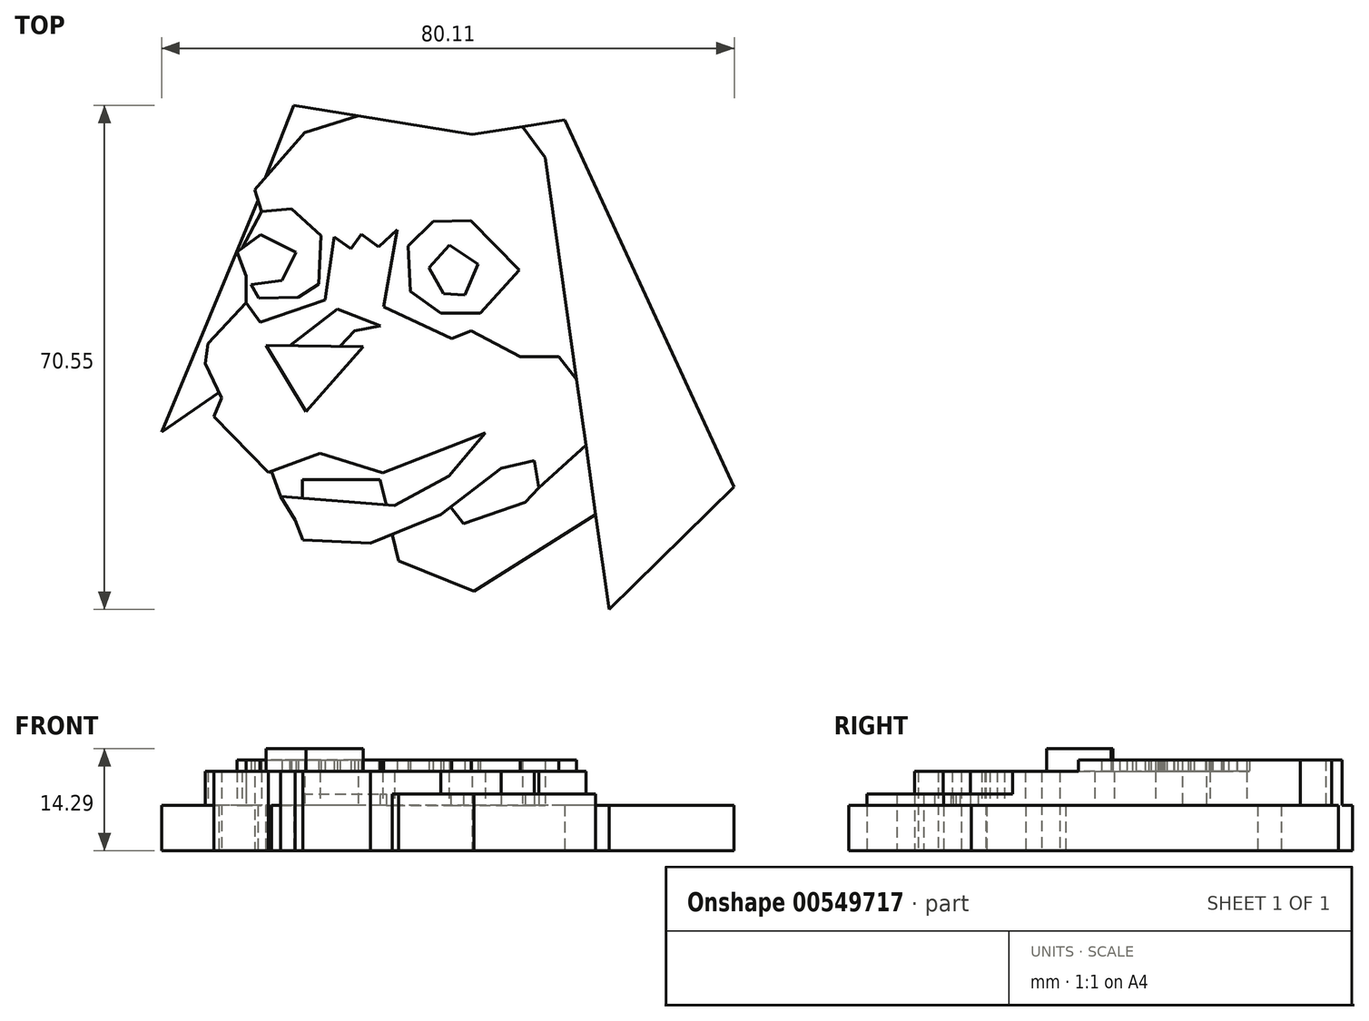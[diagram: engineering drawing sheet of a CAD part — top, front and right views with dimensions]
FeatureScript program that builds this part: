
annotation { "Feature Type Name" : "Feature", "Feature Type Description" : "" }
export const myFeature = defineFeature(function(context is Context, id is Id, definition is map)
    precondition{}
    {
        {
            var Q0;
            Q0=qCreatedBy(makeId("Top.planeOp"),FACE);
            var sketch = newSketch(context, id + "F0", { "sketchPlane" : qUnion([Q0])});
            skLineSegment(sketch, "E0", {"start": v(-28.92, 19.78) * mm, "end": v(-27.96, 16.71) * mm});
            skLineSegment(sketch, "E1", {"start": v(-27.96, 16.71) * mm, "end": v(-23.77, 17.1) * mm});
            skLineSegment(sketch, "E2", {"start": v(-23.77, 17.1) * mm, "end": v(-19.66, 13.35) * mm});
            skLineSegment(sketch, "E3", {"start": v(-19.66, 13.35) * mm, "end": v(-19.93, 6.56) * mm});
            skLineSegment(sketch, "E4", {"start": v(-19.93, 6.56) * mm, "end": v(-22.81, 4.73) * mm});
            skLineSegment(sketch, "E5", {"start": v(-22.81, 4.73) * mm, "end": v(-28.35, 4.56) * mm});
            skLineSegment(sketch, "E6", {"start": v(-28.35, 4.56) * mm, "end": v(-30.1, 7.71) * mm});
            skLineSegment(sketch, "E7", {"start": v(-30.1, 7.71) * mm, "end": v(-30.1, 3.95) * mm});
            skLineSegment(sketch, "E8", {"start": v(-30.1, 7.71) * mm, "end": v(-31.36, 11.09) * mm});
            skLineSegment(sketch, "E9", {"start": v(-31.36, 11.09) * mm, "end": v(-28.1, 13.47) * mm});
            skLineSegment(sketch, "E10", {"start": v(-28.1, 13.47) * mm, "end": v(-23.11, 10.99) * mm});
            skLineSegment(sketch, "E11", {"start": v(-23.11, 10.99) * mm, "end": v(-25.06, 7.08) * mm});
            skLineSegment(sketch, "E12", {"start": v(-25.06, 7.08) * mm, "end": v(-29.42, 6.49) * mm});
            skLineSegment(sketch, "E13", {"start": v(-27.96, 16.71) * mm, "end": v(-30.7, 11.57) * mm});
            skLineSegment(sketch, "E14", {"start": v(-28.44, 18.25) * mm, "end": v(-41.92, -14.16) * mm});
            skLineSegment(sketch, "E15", {"start": v(-41.92, -14.16) * mm, "end": v(-33.9, -8.63) * mm});
            skLineSegment(sketch, "E16", {"start": v(-33.9, -8.63) * mm, "end": v(-35.81, -4.56) * mm});
            skLineSegment(sketch, "E17", {"start": v(-35.81, -4.56) * mm, "end": v(-35.46, -1.8) * mm});
            skLineSegment(sketch, "E18", {"start": v(-35.46, -1.8) * mm, "end": v(-30.1, 3.95) * mm});
            skLineSegment(sketch, "E19", {"start": v(-30.1, 3.95) * mm, "end": v(-28.12, 1.24) * mm});
            skLineSegment(sketch, "E20", {"start": v(-28.12, 1.24) * mm, "end": v(-19.08, 4.3) * mm});
            skLineSegment(sketch, "E21", {"start": v(-19.08, 4.3) * mm, "end": v(-17.81, 13.18) * mm});
            skLineSegment(sketch, "E22", {"start": v(-17.81, 13.18) * mm, "end": v(-15.44, 11.49) * mm});
            skLineSegment(sketch, "E23", {"start": v(-15.44, 11.49) * mm, "end": v(-14, 13.5) * mm});
            skLineSegment(sketch, "E24", {"start": v(-14, 13.5) * mm, "end": v(-11.55, 11.76) * mm});
            skLineSegment(sketch, "E25", {"start": v(-11.55, 11.76) * mm, "end": v(-8.94, 14.17) * mm});
            skLineSegment(sketch, "E26", {"start": v(-8.94, 14.17) * mm, "end": v(-10.88, 3.37) * mm});
            skLineSegment(sketch, "E27", {"start": v(-10.88, 3.37) * mm, "end": v(-1.34, -1.04) * mm});
            skLineSegment(sketch, "E28", {"start": v(-1.34, -1.04) * mm, "end": v(1.4, 0) * mm});
            skLineSegment(sketch, "E29", {"start": v(1.4, 0) * mm, "end": v(8.24, -3.6) * mm});
            skLineSegment(sketch, "E30", {"start": v(8.24, -3.6) * mm, "end": v(13.64, -3.6) * mm});
            skLineSegment(sketch, "E31", {"start": v(13.64, -3.6) * mm, "end": v(16.12, -6.8) * mm});
            skLineSegment(sketch, "E32", {"start": v(11.71, 24.26) * mm, "end": v(20.68, -38.98) * mm});
            skLineSegment(sketch, "E33", {"start": v(20.68, -38.98) * mm, "end": v(38.19, -21.8) * mm});
            skLineSegment(sketch, "E34", {"start": v(38.19, -21.8) * mm, "end": v(14.47, 29.55) * mm});
            skLineSegment(sketch, "E35", {"start": v(14.47, 29.55) * mm, "end": v(1.52, 27.5) * mm});
            skLineSegment(sketch, "E36", {"start": v(4.12, 27.08) * mm, "end": v(-23.44, 31.57) * mm});
            skLineSegment(sketch, "E37", {"start": v(-23.44, 31.57) * mm, "end": v(-27.48, 21.27) * mm});
            skLineSegment(sketch, "E38", {"start": v(-28.92, 19.78) * mm, "end": v(-21.91, 27.77) * mm});
            skLineSegment(sketch, "E39", {"start": v(-21.91, 27.77) * mm, "end": v(-14.43, 30.1) * mm});
            skLineSegment(sketch, "E40", {"start": v(7.07, 24.85) * mm, "end": v(11.71, 24.26) * mm});
            skLineSegment(sketch, "E41", {"start": v(-7.46, 11.9) * mm, "end": v(-3.96, 15.32) * mm});
            skLineSegment(sketch, "E42", {"start": v(-3.96, 15.32) * mm, "end": v(1.35, 15.44) * mm});
            skLineSegment(sketch, "E43", {"start": v(1.35, 15.44) * mm, "end": v(8.1, 8.52) * mm});
            skLineSegment(sketch, "E44", {"start": v(8.1, 8.52) * mm, "end": v(2.67, 2.5) * mm});
            skLineSegment(sketch, "E45", {"start": v(2.67, 2.5) * mm, "end": v(-2.9, 2.5) * mm});
            skLineSegment(sketch, "E46", {"start": v(-2.9, 2.5) * mm, "end": v(-7.12, 5.55) * mm});
            skLineSegment(sketch, "E47", {"start": v(-7.12, 5.55) * mm, "end": v(-7.46, 11.9) * mm});
            skLineSegment(sketch, "E48", {"start": v(-4.5, 8.85) * mm, "end": v(-1.65, 12) * mm});
            skLineSegment(sketch, "E49", {"start": v(-1.65, 12) * mm, "end": v(2.34, 9.35) * mm});
            skLineSegment(sketch, "E50", {"start": v(2.34, 9.35) * mm, "end": v(0.52, 5) * mm});
            skLineSegment(sketch, "E51", {"start": v(0.52, 5) * mm, "end": v(-2.48, 5.22) * mm});
            skLineSegment(sketch, "E52", {"start": v(-2.48, 5.22) * mm, "end": v(-4.5, 8.85) * mm});
            skLineSegment(sketch, "E53", {"start": v(-32.42, -6.74) * mm, "end": v(-34.61, -11.98) * mm});
            skLineSegment(sketch, "E54", {"start": v(-34.61, -11.98) * mm, "end": v(-26.99, -19.8) * mm});
            skLineSegment(sketch, "E55", {"start": v(-26.99, -19.8) * mm, "end": v(-19.76, -17.15) * mm});
            skLineSegment(sketch, "E56", {"start": v(-19.76, -17.15) * mm, "end": v(-11.02, -19.87) * mm});
            skLineSegment(sketch, "E57", {"start": v(-11.02, -19.87) * mm, "end": v(3.38, -14.27) * mm});
            skLineSegment(sketch, "E58", {"start": v(3.38, -14.27) * mm, "end": v(-1.71, -20.33) * mm});
            skLineSegment(sketch, "E59", {"start": v(-1.71, -20.33) * mm, "end": v(-9.37, -24.45) * mm});
            skLineSegment(sketch, "E60", {"start": v(-9.37, -24.45) * mm, "end": v(-25.28, -23.17) * mm});
            skLineSegment(sketch, "E61", {"start": v(-25.28, -23.17) * mm, "end": v(-26.57, -19.65) * mm});
            skLineSegment(sketch, "E62", {"start": v(-22.25, -23.41) * mm, "end": v(-22.25, -20.84) * mm});
            skLineSegment(sketch, "E63", {"start": v(-22.25, -20.84) * mm, "end": v(-11.39, -20.84) * mm});
            skLineSegment(sketch, "E64", {"start": v(-11.39, -20.84) * mm, "end": v(-10.5, -24.36) * mm});
            skLineSegment(sketch, "E65", {"start": v(-25.28, -23.17) * mm, "end": v(-23.24, -26.44) * mm});
            skLineSegment(sketch, "E66", {"start": v(-23.24, -26.44) * mm, "end": v(-22.2, -29.25) * mm});
            skLineSegment(sketch, "E67", {"start": v(-22.2, -29.25) * mm, "end": v(-12.7, -29.74) * mm});
            skLineSegment(sketch, "E68", {"start": v(-12.7, -29.74) * mm, "end": v(-2.87, -25.74) * mm});
            skLineSegment(sketch, "E69", {"start": v(-2.87, -25.74) * mm, "end": v(5.56, -19.21) * mm});
            skLineSegment(sketch, "E70", {"start": v(5.56, -19.21) * mm, "end": v(10.24, -12.1) * mm});
            skLineSegment(sketch, "E71", {"start": v(5.56, -19.21) * mm, "end": v(10.25, -18.17) * mm});
            skLineSegment(sketch, "E72", {"start": v(10.25, -18.17) * mm, "end": v(10.88, -21.95) * mm});
            skLineSegment(sketch, "E73", {"start": v(10.88, -21.95) * mm, "end": v(8.92, -23.96) * mm});
            skLineSegment(sketch, "E74", {"start": v(8.92, -23.96) * mm, "end": v(0.28, -26.95) * mm});
            skLineSegment(sketch, "E75", {"start": v(0.28, -26.95) * mm, "end": v(-1.48, -24.66) * mm});
            skLineSegment(sketch, "E76", {"start": v(10.88, -21.95) * mm, "end": v(17.42, -16.03) * mm});
            skLineSegment(sketch, "E77", {"start": v(-9.63, -28.5) * mm, "end": v(-8.76, -32.21) * mm});
            skLineSegment(sketch, "E78", {"start": v(-8.76, -32.21) * mm, "end": v(1.74, -36.41) * mm});
            skLineSegment(sketch, "E79", {"start": v(1.74, -36.41) * mm, "end": v(18.8, -25.7) * mm});
            skLineSegment(sketch, "E80", {"start": v(-21.73, -11.3) * mm, "end": v(-13.7, -2.22) * mm});
            skLineSegment(sketch, "E81", {"start": v(-13.7, -2.22) * mm, "end": v(-27.3, -2) * mm});
            skLineSegment(sketch, "E82", {"start": v(-27.3, -2) * mm, "end": v(-21.73, -11.3) * mm});
            skLineSegment(sketch, "E83", {"start": v(-17.31, 3.04) * mm, "end": v(-24, -2.06) * mm});
            skLineSegment(sketch, "E84", {"start": v(-17.31, 3.04) * mm, "end": v(-11.32, 0.74) * mm});
            skLineSegment(sketch, "E85", {"start": v(-11.32, 0.74) * mm, "end": v(-14.94, 0) * mm});
            skLineSegment(sketch, "E86", {"start": v(-14.94, 0) * mm, "end": v(-16.95, -2.17) * mm});
            skLineSegment(sketch, "E87", {"start": v(-33.9, -8.63) * mm, "end": v(-33.54, -9.41) * mm});
            skLineSegment(sketch, "E88", {"start": v(11.71, 24.26) * mm, "end": v(8.56, 28.61) * mm});
            skSolve(sketch);
        }
        {
            var Q0;
            {var subQ0=sQuery(id+"F0.wireOp",EDGE,"E33");Q0=makeQuery(id+"F0.imprint","IMPRINT",FACE,{"disambiguationData":[TD([[makeQuery(id+"F0.imprint","IMPRINT",EDGE,{"derivedFrom":subQ0}),1.0]])]});}
            var Q1;
            {var subQ3=sQuery(id+"F0.wireOp",EDGE,"E39");Q1=makeQuery(id+"F0.imprint","IMPRINT",FACE,{"disambiguationData":[TD([[makeQuery(id+"F0.imprint","IMPRINT",EDGE,{"derivedFrom":subQ3}),1.0]])]});}
            var Q2;
            Q2=makeQuery(id+"F0.imprint","IMPRINT",FACE,{"disambiguationData":[TD([[makeQuery(id+"F0.imprint","IMPRINT",EDGE,{"derivedFrom":sQuery(id+"F0.wireOp",EDGE,"E7")}),-1.0]])]});
            var Q3;
            {var subQ0=sQuery(id+"F0.wireOp",EDGE,"E1");Q3=makeQuery(id+"F0.imprint","IMPRINT",FACE,{"disambiguationData":[TD([[makeQuery(id+"F0.imprint","IMPRINT",EDGE,{"derivedFrom":subQ0}),1.0]])]});}
            var Q4;
            Q4=makeQuery(id+"F0.imprint","IMPRINT",FACE,{"disambiguationData":[TD([[makeQuery(id+"F0.imprint","IMPRINT",EDGE,{"derivedFrom":sQuery(id+"F0.wireOp",EDGE,"E1")}),-1.0]])]});
            var Q5;
            {var subQ3=sQuery(id+"F0.wireOp",EDGE,"E8");Q5=makeQuery(id+"F0.imprint","IMPRINT",FACE,{"disambiguationData":[TD([[makeQuery(id+"F0.imprint","IMPRINT",EDGE,{"derivedFrom":subQ3}),-1.0]])]});}
            var Q6;
            Q6=makeQuery(id+"F0.imprint","IMPRINT",FACE,{"disambiguationData":[TD([[makeQuery(id+"F0.imprint","IMPRINT",EDGE,{"derivedFrom":sQuery(id+"F0.wireOp",EDGE,"E48")}),-1.0]])]});
            var Q7;
            Q7=makeQuery(id+"F0.imprint","IMPRINT",FACE,{"disambiguationData":[TD([[makeQuery(id+"F0.imprint","IMPRINT",EDGE,{"derivedFrom":sQuery(id+"F0.wireOp",EDGE,"E41")}),-1.0]])]});
            var Q8;
            Q8=makeQuery(id+"F0.imprint","IMPRINT",FACE,{"disambiguationData":[TD([[makeQuery(id+"F0.imprint","IMPRINT",EDGE,{"derivedFrom":sQuery(id+"F0.wireOp",EDGE,"E16")}),-1.0]])]});
            var Q9;
            {var subQ4=sQuery(id+"F0.wireOp",EDGE,"E80");Q9=makeQuery(id+"F0.imprint","IMPRINT",FACE,{"disambiguationData":[TD([[makeQuery(id+"F0.imprint","IMPRINT",EDGE,{"derivedFrom":subQ4}),1.0]])]});}
            var Q10;
            {var subQ0=sQuery(id+"F0.wireOp",EDGE,"E83");Q10=makeQuery(id+"F0.imprint","IMPRINT",FACE,{"disambiguationData":[TD([[makeQuery(id+"F0.imprint","IMPRINT",EDGE,{"derivedFrom":subQ0}),1.0]])]});}
            var Q11;
            {var subQ5=sQuery(id+"F0.wireOp",EDGE,"E56");Q11=makeQuery(id+"F0.imprint","IMPRINT",FACE,{"disambiguationData":[TD([[makeQuery(id+"F0.imprint","IMPRINT",EDGE,{"derivedFrom":subQ5}),-1.0]])]});}
            var Q12;
            {var subQ0=sQuery(id+"F0.wireOp",EDGE,"E62");Q12=makeQuery(id+"F0.imprint","IMPRINT",FACE,{"disambiguationData":[TD([[makeQuery(id+"F0.imprint","IMPRINT",EDGE,{"derivedFrom":subQ0}),-1.0]])]});}
            var Q13;
            {var subQ0=sQuery(id+"F0.wireOp",EDGE,"E71");Q13=makeQuery(id+"F0.imprint","IMPRINT",FACE,{"disambiguationData":[TD([[makeQuery(id+"F0.imprint","IMPRINT",EDGE,{"derivedFrom":subQ0}),-1.0]])]});}
            var Q14;
            Q14=makeQuery(id+"F0.imprint","IMPRINT",FACE,{"disambiguationData":[TD([[makeQuery(id+"F0.imprint","IMPRINT",EDGE,{"derivedFrom":sQuery(id+"F0.wireOp",EDGE,"E73")}),1.0]])]});
            extrude(context, id + "F1", {"entities" : qUnion([Q0, Q1, Q2, Q3, Q4, Q5, Q6, Q7, Q8, Q9, Q10, Q11, Q12, Q13, Q14]), "depth" : 6.35 * mm, "offsetDistance" : 25.4 * mm});
        }
        {
            var Q0;
            Q0=makeQuery(id+"F0.imprint","IMPRINT",FACE,{"disambiguationData":[TD([[makeQuery(id+"F0.imprint","IMPRINT",EDGE,{"derivedFrom":sQuery(id+"F0.wireOp",EDGE,"E16")}),-1.0]])]});
            var Q1;
            {var subQ0=sQuery(id+"F0.wireOp",EDGE,"E1");Q1=makeQuery(id+"F0.imprint","IMPRINT",FACE,{"disambiguationData":[TD([[makeQuery(id+"F0.imprint","IMPRINT",EDGE,{"derivedFrom":subQ0}),1.0]])]});}
            var Q2;
            {var subQ0=sQuery(id+"F0.wireOp",EDGE,"E62");Q2=makeQuery(id+"F0.imprint","IMPRINT",FACE,{"disambiguationData":[TD([[makeQuery(id+"F0.imprint","IMPRINT",EDGE,{"derivedFrom":subQ0}),-1.0]])]});}
            var Q3;
            {var subQ3=sQuery(id+"F0.wireOp",EDGE,"E8");Q3=makeQuery(id+"F0.imprint","IMPRINT",FACE,{"disambiguationData":[TD([[makeQuery(id+"F0.imprint","IMPRINT",EDGE,{"derivedFrom":subQ3}),-1.0]])]});}
            var Q4;
            Q4=makeQuery(id+"F0.imprint","IMPRINT",FACE,{"disambiguationData":[TD([[makeQuery(id+"F0.imprint","IMPRINT",EDGE,{"derivedFrom":sQuery(id+"F0.wireOp",EDGE,"E48")}),-1.0]])]});
            var Q5;
            {var subQ0=sQuery(id+"F0.wireOp",EDGE,"E83");Q5=makeQuery(id+"F0.imprint","IMPRINT",FACE,{"disambiguationData":[TD([[makeQuery(id+"F0.imprint","IMPRINT",EDGE,{"derivedFrom":subQ0}),1.0]])]});}
            var Q6;
            {var subQ4=sQuery(id+"F0.wireOp",EDGE,"E80");Q6=makeQuery(id+"F0.imprint","IMPRINT",FACE,{"disambiguationData":[TD([[makeQuery(id+"F0.imprint","IMPRINT",EDGE,{"derivedFrom":subQ4}),1.0]])]});}
            var Q7;
            Q7=makeQuery(id+"F0.imprint","IMPRINT",FACE,{"disambiguationData":[TD([[makeQuery(id+"F0.imprint","IMPRINT",EDGE,{"derivedFrom":sQuery(id+"F0.wireOp",EDGE,"E73")}),1.0]])]});
            extrude(context, id + "F2", {"entities" : qUnion([Q0, Q1, Q2, Q3, Q4, Q5, Q6, Q7]), "operationType" : NewBodyOperationType.ADD, "depth" : 7.94 * mm, "offsetDistance" : 25.4 * mm});
        }
        {
            var Q0;
            Q0=makeQuery(id+"F0.imprint","IMPRINT",FACE,{"disambiguationData":[TD([[makeQuery(id+"F0.imprint","IMPRINT",EDGE,{"derivedFrom":sQuery(id+"F0.wireOp",EDGE,"E16")}),-1.0]])]});
            var Q1;
            {var subQ4=sQuery(id+"F0.wireOp",EDGE,"E80");Q1=makeQuery(id+"F0.imprint","IMPRINT",FACE,{"disambiguationData":[TD([[makeQuery(id+"F0.imprint","IMPRINT",EDGE,{"derivedFrom":subQ4}),1.0]])]});}
            var Q2;
            {var subQ0=sQuery(id+"F0.wireOp",EDGE,"E83");Q2=makeQuery(id+"F0.imprint","IMPRINT",FACE,{"disambiguationData":[TD([[makeQuery(id+"F0.imprint","IMPRINT",EDGE,{"derivedFrom":subQ0}),1.0]])]});}
            var Q3;
            {var subQ0=sQuery(id+"F0.wireOp",EDGE,"E1");Q3=makeQuery(id+"F0.imprint","IMPRINT",FACE,{"disambiguationData":[TD([[makeQuery(id+"F0.imprint","IMPRINT",EDGE,{"derivedFrom":subQ0}),1.0]])]});}
            var Q4;
            {var subQ3=sQuery(id+"F0.wireOp",EDGE,"E8");Q4=makeQuery(id+"F0.imprint","IMPRINT",FACE,{"disambiguationData":[TD([[makeQuery(id+"F0.imprint","IMPRINT",EDGE,{"derivedFrom":subQ3}),-1.0]])]});}
            var Q5;
            Q5=makeQuery(id+"F0.imprint","IMPRINT",FACE,{"disambiguationData":[TD([[makeQuery(id+"F0.imprint","IMPRINT",EDGE,{"derivedFrom":sQuery(id+"F0.wireOp",EDGE,"E1")}),-1.0]])]});
            var Q6;
            Q6=makeQuery(id+"F0.imprint","IMPRINT",FACE,{"disambiguationData":[TD([[makeQuery(id+"F0.imprint","IMPRINT",EDGE,{"derivedFrom":sQuery(id+"F0.wireOp",EDGE,"E48")}),-1.0]])]});
            var Q7;
            Q7=makeQuery(id+"F0.imprint","IMPRINT",FACE,{"disambiguationData":[TD([[makeQuery(id+"F0.imprint","IMPRINT",EDGE,{"derivedFrom":sQuery(id+"F0.wireOp",EDGE,"E41")}),-1.0]])]});
            extrude(context, id + "F3", {"entities" : qUnion([Q0, Q1, Q2, Q3, Q4, Q5, Q6, Q7]), "operationType" : NewBodyOperationType.ADD, "depth" : 9.52 * mm, "offsetDistance" : 25.4 * mm});
        }
        {
            var Q0;
            Q0=makeQuery(id+"F0.imprint","IMPRINT",FACE,{"disambiguationData":[TD([[makeQuery(id+"F0.imprint","IMPRINT",EDGE,{"derivedFrom":sQuery(id+"F0.wireOp",EDGE,"E16")}),-1.0]])]});
            var Q1;
            {var subQ4=sQuery(id+"F0.wireOp",EDGE,"E80");Q1=makeQuery(id+"F0.imprint","IMPRINT",FACE,{"disambiguationData":[TD([[makeQuery(id+"F0.imprint","IMPRINT",EDGE,{"derivedFrom":subQ4}),1.0]])]});}
            var Q2;
            {var subQ0=sQuery(id+"F0.wireOp",EDGE,"E83");Q2=makeQuery(id+"F0.imprint","IMPRINT",FACE,{"disambiguationData":[TD([[makeQuery(id+"F0.imprint","IMPRINT",EDGE,{"derivedFrom":subQ0}),1.0]])]});}
            var Q3;
            {var subQ0=sQuery(id+"F0.wireOp",EDGE,"E1");Q3=makeQuery(id+"F0.imprint","IMPRINT",FACE,{"disambiguationData":[TD([[makeQuery(id+"F0.imprint","IMPRINT",EDGE,{"derivedFrom":subQ0}),1.0]])]});}
            var Q4;
            {var subQ3=sQuery(id+"F0.wireOp",EDGE,"E8");Q4=makeQuery(id+"F0.imprint","IMPRINT",FACE,{"disambiguationData":[TD([[makeQuery(id+"F0.imprint","IMPRINT",EDGE,{"derivedFrom":subQ3}),-1.0]])]});}
            var Q5;
            Q5=makeQuery(id+"F0.imprint","IMPRINT",FACE,{"disambiguationData":[TD([[makeQuery(id+"F0.imprint","IMPRINT",EDGE,{"derivedFrom":sQuery(id+"F0.wireOp",EDGE,"E48")}),-1.0]])]});
            extrude(context, id + "F4", {"entities" : qUnion([Q0, Q1, Q2, Q3, Q4, Q5]), "operationType" : NewBodyOperationType.ADD, "depth" : 11.1 * mm, "offsetDistance" : 25.4 * mm});
        }
        {
            var Q0;
            {var subQ0=sQuery(id+"F0.wireOp",EDGE,"E1");Q0=makeQuery(id+"F0.imprint","IMPRINT",FACE,{"disambiguationData":[TD([[makeQuery(id+"F0.imprint","IMPRINT",EDGE,{"derivedFrom":subQ0}),1.0]])]});}
            var Q1;
            {var subQ0=sQuery(id+"F0.wireOp",EDGE,"E83");Q1=makeQuery(id+"F0.imprint","IMPRINT",FACE,{"disambiguationData":[TD([[makeQuery(id+"F0.imprint","IMPRINT",EDGE,{"derivedFrom":subQ0}),1.0]])]});}
            var Q2;
            {var subQ4=sQuery(id+"F0.wireOp",EDGE,"E80");Q2=makeQuery(id+"F0.imprint","IMPRINT",FACE,{"disambiguationData":[TD([[makeQuery(id+"F0.imprint","IMPRINT",EDGE,{"derivedFrom":subQ4}),1.0]])]});}
            extrude(context, id + "F5", {"entities" : qUnion([Q0, Q1, Q2]), "operationType" : NewBodyOperationType.ADD, "depth" : 12.7 * mm, "offsetDistance" : 25.4 * mm});
        }
        {
            var Q0;
            {var subQ4=sQuery(id+"F0.wireOp",EDGE,"E80");Q0=makeQuery(id+"F0.imprint","IMPRINT",FACE,{"disambiguationData":[TD([[makeQuery(id+"F0.imprint","IMPRINT",EDGE,{"derivedFrom":subQ4}),1.0]])]});}
            extrude(context, id + "F6", {"entities" : qUnion([Q0]), "operationType" : NewBodyOperationType.ADD, "depth" : 14.29 * mm, "offsetDistance" : 25.4 * mm});
        }
        {
            var Q0;
            {var subQ0=sQuery(id+"F0.wireOp",EDGE,"E9");var subQ1=sQuery(id+"F0.wireOp",EDGE,"E8");var subQ2=sQuery(id+"F0.wireOp",EDGE,"E7");var subQ3=sQuery(id+"F0.wireOp",EDGE,"E6");var subQ4=sQuery(id+"F0.wireOp",EDGE,"E10");var subQ5=sQuery(id+"F0.wireOp",EDGE,"E11");var subQ6=sQuery(id+"F0.wireOp",EDGE,"E12");Q0=makeQuery(id+"F5.boolean.opBoolean","SPLIT",FACE,{"disambiguationData":[TD([makeQuery(id+"F2.opExtrude","SWEPT_FACE",FACE,{"disambiguationData":[OSD([subQ1])]})])],"derivedFrom":makeQuery(id+"F4.opExtrude","CAP_FACE",FACE,{"disambiguationData":[OSD([sQuery(id+"F0.wireOp",EDGE,"E0"),sQuery(id+"F0.wireOp",EDGE,"E1"),sQuery(id+"F0.wireOp",EDGE,"E2"),sQuery(id+"F0.wireOp",EDGE,"E3"),sQuery(id+"F0.wireOp",EDGE,"E4"),sQuery(id+"F0.wireOp",EDGE,"E5"),subQ3,subQ2,subQ1,subQ0,subQ4,subQ5,subQ6,sQuery(id+"F0.wireOp",EDGE,"E16"),sQuery(id+"F0.wireOp",EDGE,"E17"),sQuery(id+"F0.wireOp",EDGE,"E18"),sQuery(id+"F0.wireOp",EDGE,"E32"),sQuery(id+"F0.wireOp",EDGE,"E35"),sQuery(id+"F0.wireOp",EDGE,"E36"),sQuery(id+"F0.wireOp",EDGE,"E38"),sQuery(id+"F0.wireOp",EDGE,"E39"),sQuery(id+"F0.wireOp",EDGE,"E41"),sQuery(id+"F0.wireOp",EDGE,"E42"),sQuery(id+"F0.wireOp",EDGE,"E43"),sQuery(id+"F0.wireOp",EDGE,"E44"),sQuery(id+"F0.wireOp",EDGE,"E45"),sQuery(id+"F0.wireOp",EDGE,"E46"),sQuery(id+"F0.wireOp",EDGE,"E47"),sQuery(id+"F0.wireOp",EDGE,"E53"),sQuery(id+"F0.wireOp",EDGE,"E54"),sQuery(id+"F0.wireOp",EDGE,"E55"),sQuery(id+"F0.wireOp",EDGE,"E56"),sQuery(id+"F0.wireOp",EDGE,"E57"),sQuery(id+"F0.wireOp",EDGE,"E58"),sQuery(id+"F0.wireOp",EDGE,"E59"),sQuery(id+"F0.wireOp",EDGE,"E60"),sQuery(id+"F0.wireOp",EDGE,"E65"),sQuery(id+"F0.wireOp",EDGE,"E66"),sQuery(id+"F0.wireOp",EDGE,"E67"),sQuery(id+"F0.wireOp",EDGE,"E68"),sQuery(id+"F0.wireOp",EDGE,"E69"),sQuery(id+"F0.wireOp",EDGE,"E71"),sQuery(id+"F0.wireOp",EDGE,"E72"),sQuery(id+"F0.wireOp",EDGE,"E76"),sQuery(id+"F0.wireOp",EDGE,"E87"),sQuery(id+"F0.wireOp",EDGE,"E88")])],"isStart":false})});}
            var Q1;
            Q1=makeQuery(id+"F4.opExtrude","CAP_FACE",FACE,{"disambiguationData":[OSD([sQuery(id+"F0.wireOp",EDGE,"E48"),sQuery(id+"F0.wireOp",EDGE,"E49"),sQuery(id+"F0.wireOp",EDGE,"E50"),sQuery(id+"F0.wireOp",EDGE,"E51"),sQuery(id+"F0.wireOp",EDGE,"E52")])],"isStart":false});
            var Q2;
            Q2=makeQuery(id+"F5.opExtrude","CAP_FACE",FACE,{"disambiguationData":[OSD([sQuery(id+"F0.wireOp",EDGE,"E80"),sQuery(id+"F0.wireOp",EDGE,"E81"),sQuery(id+"F0.wireOp",EDGE,"E82"),sQuery(id+"F0.wireOp",EDGE,"E83"),sQuery(id+"F0.wireOp",EDGE,"E84"),sQuery(id+"F0.wireOp",EDGE,"E85"),sQuery(id+"F0.wireOp",EDGE,"E86")])],"isStart":false});
            extrude(context, id + "F7", {"entities" : qUnion([Q0, Q1]), "operationType" : NewBodyOperationType.ADD, "endBound" : BoundingType.UP_TO_SURFACE, "depth" : 25.4 * mm, "endBoundEntityFace" : qUnion([Q2]), "offsetDistance" : 25.4 * mm});
        }
        {
            var Q0;
            {var subQ0=sQuery(id+"F0.wireOp",EDGE,"E0");var subQ1=sQuery(id+"F0.wireOp",EDGE,"E13");var subQ2=sQuery(id+"F0.wireOp",EDGE,"E9");Q0=makeQuery(id+"F4.boolean.opBoolean","SPLIT",FACE,{"disambiguationData":[TD([makeQuery(id+"F1.opExtrude","SWEPT_FACE",FACE,{"disambiguationData":[OSD([subQ0])]})])],"derivedFrom":makeQuery(id+"F3.opExtrude","CAP_FACE",FACE,{"disambiguationData":[OSD([subQ0,sQuery(id+"F0.wireOp",EDGE,"E7"),sQuery(id+"F0.wireOp",EDGE,"E8"),subQ2,subQ1,sQuery(id+"F0.wireOp",EDGE,"E16"),sQuery(id+"F0.wireOp",EDGE,"E17"),sQuery(id+"F0.wireOp",EDGE,"E18"),sQuery(id+"F0.wireOp",EDGE,"E32"),sQuery(id+"F0.wireOp",EDGE,"E35"),sQuery(id+"F0.wireOp",EDGE,"E36"),sQuery(id+"F0.wireOp",EDGE,"E38"),sQuery(id+"F0.wireOp",EDGE,"E39"),sQuery(id+"F0.wireOp",EDGE,"E53"),sQuery(id+"F0.wireOp",EDGE,"E54"),sQuery(id+"F0.wireOp",EDGE,"E55"),sQuery(id+"F0.wireOp",EDGE,"E56"),sQuery(id+"F0.wireOp",EDGE,"E57"),sQuery(id+"F0.wireOp",EDGE,"E58"),sQuery(id+"F0.wireOp",EDGE,"E59"),sQuery(id+"F0.wireOp",EDGE,"E60"),sQuery(id+"F0.wireOp",EDGE,"E65"),sQuery(id+"F0.wireOp",EDGE,"E66"),sQuery(id+"F0.wireOp",EDGE,"E67"),sQuery(id+"F0.wireOp",EDGE,"E68"),sQuery(id+"F0.wireOp",EDGE,"E69"),sQuery(id+"F0.wireOp",EDGE,"E71"),sQuery(id+"F0.wireOp",EDGE,"E72"),sQuery(id+"F0.wireOp",EDGE,"E76"),sQuery(id+"F0.wireOp",EDGE,"E87"),sQuery(id+"F0.wireOp",EDGE,"E88")])],"isStart":false})});}
            var Q1;
            Q1=makeQuery(id+"F4.boolean.opBoolean","SPLIT",FACE,{"disambiguationData":[TD([makeQuery(id+"F4.opExtrude","SWEPT_FACE",FACE,{"disambiguationData":[OSD([sQuery(id+"F0.wireOp",EDGE,"E41")])]})])],"derivedFrom":makeQuery(id+"F3.opExtrude","CAP_FACE",FACE,{"disambiguationData":[OSD([sQuery(id+"F0.wireOp",EDGE,"E0"),sQuery(id+"F0.wireOp",EDGE,"E7"),sQuery(id+"F0.wireOp",EDGE,"E8"),sQuery(id+"F0.wireOp",EDGE,"E9"),sQuery(id+"F0.wireOp",EDGE,"E13"),sQuery(id+"F0.wireOp",EDGE,"E16"),sQuery(id+"F0.wireOp",EDGE,"E17"),sQuery(id+"F0.wireOp",EDGE,"E18"),sQuery(id+"F0.wireOp",EDGE,"E32"),sQuery(id+"F0.wireOp",EDGE,"E35"),sQuery(id+"F0.wireOp",EDGE,"E36"),sQuery(id+"F0.wireOp",EDGE,"E38"),sQuery(id+"F0.wireOp",EDGE,"E39"),sQuery(id+"F0.wireOp",EDGE,"E53"),sQuery(id+"F0.wireOp",EDGE,"E54"),sQuery(id+"F0.wireOp",EDGE,"E55"),sQuery(id+"F0.wireOp",EDGE,"E56"),sQuery(id+"F0.wireOp",EDGE,"E57"),sQuery(id+"F0.wireOp",EDGE,"E58"),sQuery(id+"F0.wireOp",EDGE,"E59"),sQuery(id+"F0.wireOp",EDGE,"E60"),sQuery(id+"F0.wireOp",EDGE,"E65"),sQuery(id+"F0.wireOp",EDGE,"E66"),sQuery(id+"F0.wireOp",EDGE,"E67"),sQuery(id+"F0.wireOp",EDGE,"E68"),sQuery(id+"F0.wireOp",EDGE,"E69"),sQuery(id+"F0.wireOp",EDGE,"E71"),sQuery(id+"F0.wireOp",EDGE,"E72"),sQuery(id+"F0.wireOp",EDGE,"E76"),sQuery(id+"F0.wireOp",EDGE,"E87"),sQuery(id+"F0.wireOp",EDGE,"E88")])],"isStart":false})});
            var Q2;
            {var subQ0=sQuery(id+"F0.wireOp",EDGE,"E68");var subQ1=sQuery(id+"F0.wireOp",EDGE,"E54");var subQ2=sQuery(id+"F0.wireOp",EDGE,"E67");var subQ3=sQuery(id+"F0.wireOp",EDGE,"E53");var subQ4=sQuery(id+"F0.wireOp",EDGE,"E66");var subQ5=sQuery(id+"F0.wireOp",EDGE,"E65");var subQ6=sQuery(id+"F0.wireOp",EDGE,"E60");var subQ7=sQuery(id+"F0.wireOp",EDGE,"E59");var subQ8=sQuery(id+"F0.wireOp",EDGE,"E7");var subQ9=sQuery(id+"F0.wireOp",EDGE,"E58");var subQ10=sQuery(id+"F0.wireOp",EDGE,"E57");var subQ11=sQuery(id+"F0.wireOp",EDGE,"E56");var subQ12=sQuery(id+"F0.wireOp",EDGE,"E55");var subQ13=sQuery(id+"F0.wireOp",EDGE,"E32");var subQ14=sQuery(id+"F0.wireOp",EDGE,"E18");var subQ15=sQuery(id+"F0.wireOp",EDGE,"E17");var subQ16=sQuery(id+"F0.wireOp",EDGE,"E87");var subQ17=sQuery(id+"F0.wireOp",EDGE,"E16");var subQ18=sQuery(id+"F0.wireOp",EDGE,"E72");var subQ19=sQuery(id+"F0.wireOp",EDGE,"E71");var subQ20=sQuery(id+"F0.wireOp",EDGE,"E69");var subQ21=sQuery(id+"F0.wireOp",EDGE,"E76");Q2=makeQuery(id+"F5.boolean.opBoolean","SPLIT",FACE,{"disambiguationData":[TD([makeQuery(id+"F1.opExtrude","SWEPT_FACE",FACE,{"disambiguationData":[OSD([subQ3])]})])],"derivedFrom":makeQuery(id+"F4.opExtrude","CAP_FACE",FACE,{"disambiguationData":[OSD([sQuery(id+"F0.wireOp",EDGE,"E0"),sQuery(id+"F0.wireOp",EDGE,"E1"),sQuery(id+"F0.wireOp",EDGE,"E2"),sQuery(id+"F0.wireOp",EDGE,"E3"),sQuery(id+"F0.wireOp",EDGE,"E4"),sQuery(id+"F0.wireOp",EDGE,"E5"),sQuery(id+"F0.wireOp",EDGE,"E6"),subQ8,sQuery(id+"F0.wireOp",EDGE,"E8"),sQuery(id+"F0.wireOp",EDGE,"E9"),sQuery(id+"F0.wireOp",EDGE,"E10"),sQuery(id+"F0.wireOp",EDGE,"E11"),sQuery(id+"F0.wireOp",EDGE,"E12"),subQ17,subQ15,subQ14,subQ13,sQuery(id+"F0.wireOp",EDGE,"E35"),sQuery(id+"F0.wireOp",EDGE,"E36"),sQuery(id+"F0.wireOp",EDGE,"E38"),sQuery(id+"F0.wireOp",EDGE,"E39"),sQuery(id+"F0.wireOp",EDGE,"E41"),sQuery(id+"F0.wireOp",EDGE,"E42"),sQuery(id+"F0.wireOp",EDGE,"E43"),sQuery(id+"F0.wireOp",EDGE,"E44"),sQuery(id+"F0.wireOp",EDGE,"E45"),sQuery(id+"F0.wireOp",EDGE,"E46"),sQuery(id+"F0.wireOp",EDGE,"E47"),subQ3,subQ1,subQ12,subQ11,subQ10,subQ9,subQ7,subQ6,subQ5,subQ4,subQ2,subQ0,subQ20,subQ19,subQ18,subQ21,subQ16,sQuery(id+"F0.wireOp",EDGE,"E88")])],"isStart":false})});}
            extrude(context, id + "F8", {"entities" : qUnion([Q0, Q1]), "operationType" : NewBodyOperationType.ADD, "endBound" : BoundingType.UP_TO_SURFACE, "depth" : 25.4 * mm, "endBoundEntityFace" : qUnion([Q2]), "offsetDistance" : 25.4 * mm});
        }
    });
